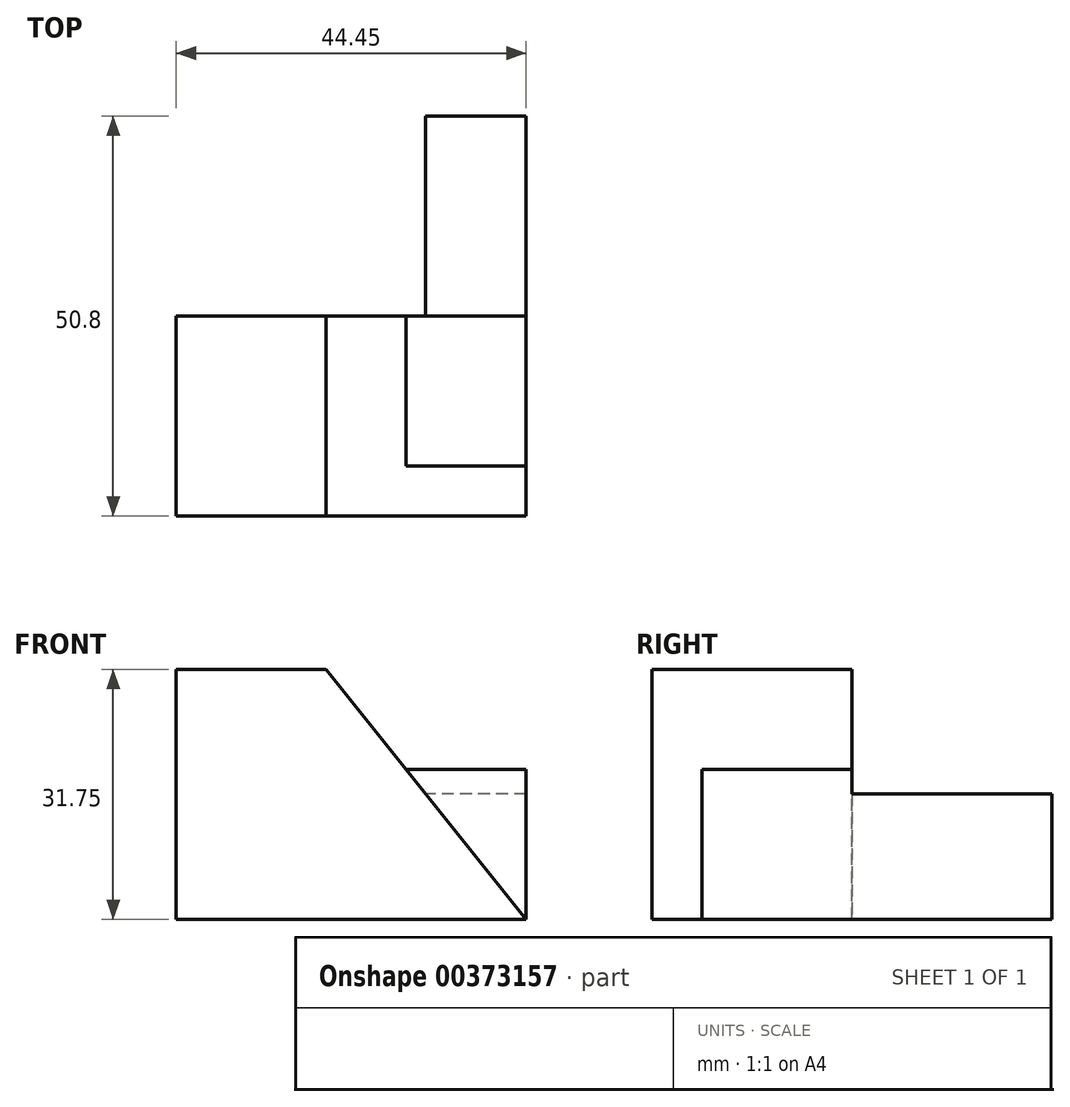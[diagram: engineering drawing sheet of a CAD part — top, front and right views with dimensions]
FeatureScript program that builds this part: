
annotation { "Feature Type Name" : "Feature", "Feature Type Description" : "" }
export const myFeature = defineFeature(function(context is Context, id is Id, definition is map)
    precondition{}
    {
        {
            var Q0;
            Q0=qCreatedBy(makeId("Front.planeOp"),FACE);
            var sketch = newSketch(context, id + "F0", { "sketchPlane" : qUnion([Q0])});
            skLineSegment(sketch, "E0", {"start": v(0, 0) * mm, "end": v(0, 31.75) * mm});
            skLineSegment(sketch, "E1", {"start": v(0, 31.75) * mm, "end": v(19.05, 31.75) * mm});
            skLineSegment(sketch, "E2", {"start": v(19.05, 31.75) * mm, "end": v(44.45, 0) * mm});
            skLineSegment(sketch, "E3", {"start": v(44.45, 0) * mm, "end": v(0, 0) * mm});
            skSolve(sketch);
        }
        {
            var Q0;
            Q0=makeQuery(id+"F0.imprint","IMPRINT",FACE,{"disambiguationData":[TD([[makeQuery(id+"F0.imprint","IMPRINT",EDGE,{"derivedFrom":sQuery(id+"F0.wireOp",EDGE,"E0")}),-1.0]])]});
            extrude(context, id + "F1", {"entities" : qUnion([Q0]), "depth" : 25.4 * mm});
        }
        {
            var Q0;
            Q0=makeQuery(id+"F1.opExtrude","CAP_FACE",FACE,{"disambiguationData":[OSD([sQuery(id+"F0.wireOp",EDGE,"E0"),sQuery(id+"F0.wireOp",EDGE,"E1"),sQuery(id+"F0.wireOp",EDGE,"E2"),sQuery(id+"F0.wireOp",EDGE,"E3")])],"isStart":true});
            var sketch = newSketch(context, id + "F2", { "sketchPlane" : qUnion([Q0])});
            skLineSegment(sketch, "E4", {"start": v(-44.45, 0) * mm, "end": v(-44.45, 15.94) * mm});
            skLineSegment(sketch, "E5", {"start": v(-44.45, 15.94) * mm, "end": v(-31.7, 15.94) * mm});
            skSolve(sketch);
        }
        {
            var Q0;
            {var subQ0=sQuery(id+"F2.wireOp",EDGE,"E4");Q0=makeQuery(id+"F2.imprint","IMPRINT",FACE,{"disambiguationData":[TD([[makeQuery(id+"F2.imprint","IMPRINT",EDGE,{"derivedFrom":subQ0}),-1.0]])]});}
            extrude(context, id + "F3", {"entities" : qUnion([Q0]), "operationType" : NewBodyOperationType.ADD, "depth" : 25.4 * mm});
        }
        {
            var Q0;
            Q0=makeQuery(id+"F1.opExtrude","CAP_FACE",FACE,{"disambiguationData":[OSD([sQuery(id+"F0.wireOp",EDGE,"E0"),sQuery(id+"F0.wireOp",EDGE,"E1"),sQuery(id+"F0.wireOp",EDGE,"E2"),sQuery(id+"F0.wireOp",EDGE,"E3")])],"isStart":true});
            var sketch = newSketch(context, id + "F4", { "sketchPlane" : qUnion([Q0])});
            skLineSegment(sketch, "E6", {"start": v(-44.45, 0) * mm, "end": v(-44.45, 19.05) * mm});
            skLineSegment(sketch, "E7", {"start": v(-44.45, 19.05) * mm, "end": v(-29.2, 19.05) * mm});
            skLineSegment(sketch, "E8", {"start": v(-29.21, 19.05) * mm, "end": v(-44.45, 0) * mm});
            skSolve(sketch);
        }
        {
            var Q0;
            Q0 = qSketchRegion(id + "F4", true);
            extrude(context, id + "F5", {"entities" : qUnion([Q0]), "operationType" : NewBodyOperationType.ADD, "oppositeDirection" : true, "depth" : 19.05 * mm});
        }
    });
